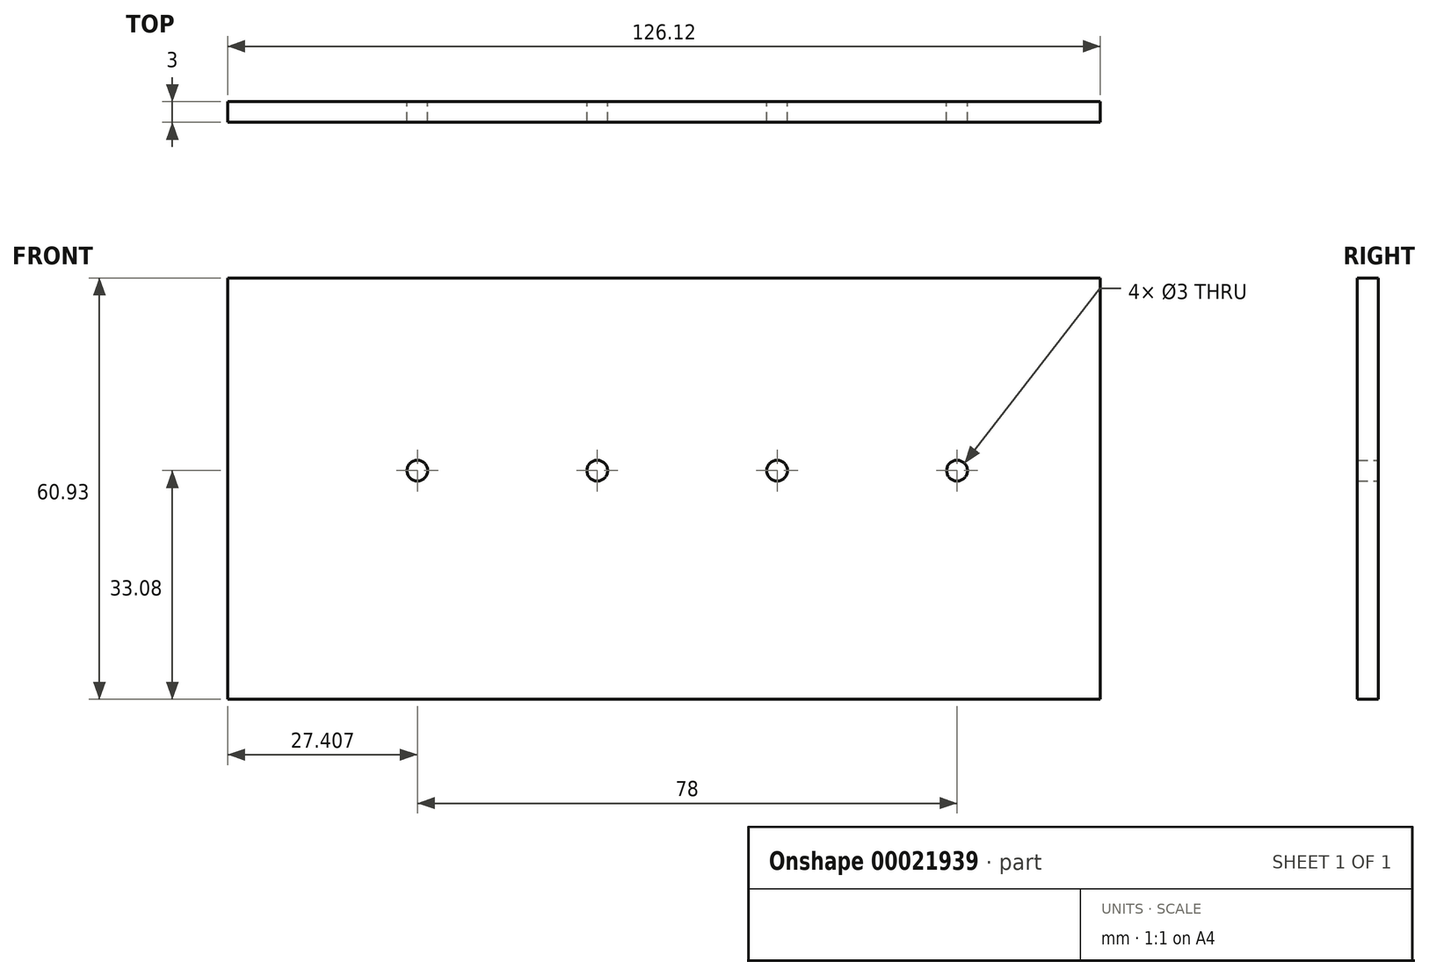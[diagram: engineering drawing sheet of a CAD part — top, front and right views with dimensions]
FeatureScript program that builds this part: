
annotation { "Feature Type Name" : "Feature", "Feature Type Description" : "" }
export const myFeature = defineFeature(function(context is Context, id is Id, definition is map)
    precondition{}
    {
        {
            var Q0;
            Q0=qCreatedBy(makeId("Front.planeOp"),FACE);
            var sketch = newSketch(context, id + "F0", { "sketchPlane" : qUnion([Q0])});
            skPoint(sketch, "E0.rect.middle", {"position": v(0, 0) * mm});
            skCircle(sketch, "E1", {"center": v(-9.53, 0) * mm, "radius": 1.5 * mm});
            skCircle(sketch, "E2", {"center": v(16.47, 0) * mm, "radius": 1.5 * mm});
            skCircle(sketch, "E3", {"center": v(42.47, 0) * mm, "radius": 1.5 * mm});
            skCircle(sketch, "E4", {"center": v(68.47, 0) * mm, "radius": 1.5 * mm});
            skLineSegment(sketch, "E5.bottom", {"start": v(-36.94, 27.85) * mm, "end": v(89.18, 27.85) * mm});
            skLineSegment(sketch, "E5.top", {"start": v(-36.94, -33.08) * mm, "end": v(89.18, -33.08) * mm});
            skLineSegment(sketch, "E5.left", {"start": v(-36.94, 27.85) * mm, "end": v(-36.94, -33.08) * mm});
            skLineSegment(sketch, "E5.right", {"start": v(89.18, 27.85) * mm, "end": v(89.18, -33.08) * mm});
            skSolve(sketch);
        }
        {
            var Q0;
            Q0=makeQuery(id+"F0.imprint","IMPRINT",FACE,{"disambiguationData":[TD([[makeQuery(id+"F0.imprint","IMPRINT",EDGE,{"derivedFrom":sQuery(id+"F0.wireOp",EDGE,"E1")}),-1.0]])]});
            extrude(context, id + "F1", {"entities" : qUnion([Q0]), "depth" : 3 * mm});
        }
    });
